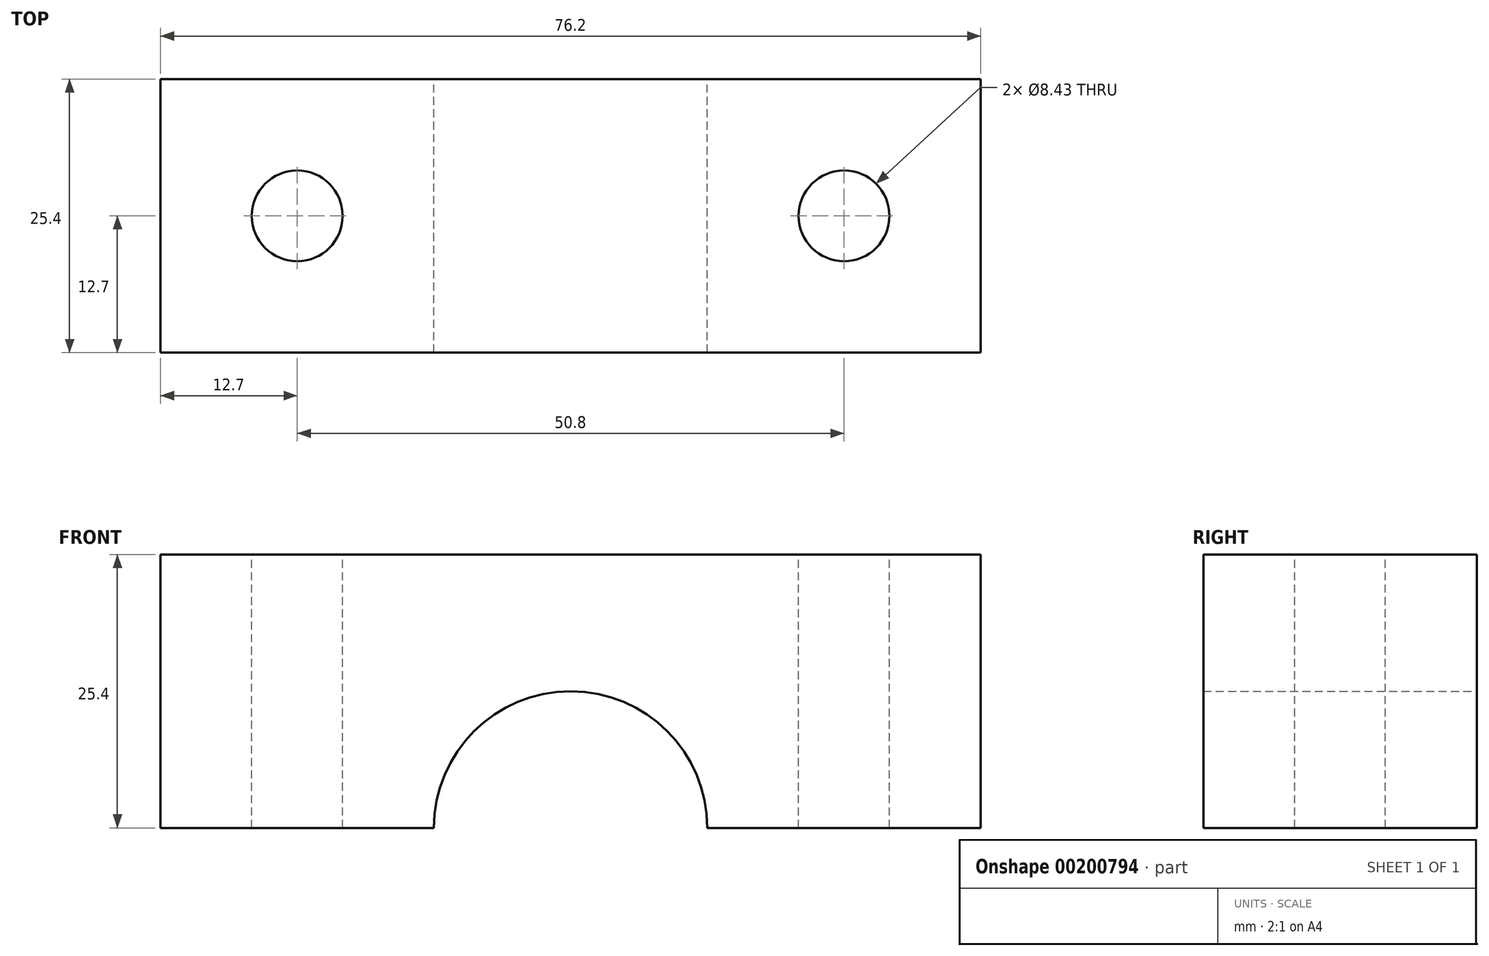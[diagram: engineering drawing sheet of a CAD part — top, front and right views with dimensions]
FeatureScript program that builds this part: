
annotation { "Feature Type Name" : "Feature", "Feature Type Description" : "" }
export const myFeature = defineFeature(function(context is Context, id is Id, definition is map)
    precondition{}
    {
        {
            var Q0;
            Q0=qCreatedBy(makeId("Front.planeOp"),FACE);
            var sketch = newSketch(context, id + "F0", { "sketchPlane" : qUnion([Q0])});
            skLineSegment(sketch, "E0.bottom", {"start": v(0, 0) * mm, "end": v(25.4, 0) * mm});
            skLineSegment(sketch, "E0.top", {"start": v(0, 25.4) * mm, "end": v(76.2, 25.4) * mm});
            skLineSegment(sketch, "E0.left", {"start": v(0, 0) * mm, "end": v(0, 25.4) * mm});
            skLineSegment(sketch, "E0.right", {"start": v(76.2, 0) * mm, "end": v(76.2, 25.4) * mm});
            skArc(sketch, "E1", {"start": v(50.8, 0) * mm, "mid": v(38.1, 12.7) * mm, "end": v(25.4, 0) * mm});
            skLineSegment(sketch, "E2.trimOffspring", {"start": v(50.8, 0) * mm, "end": v(76.2, 0) * mm});
            skSolve(sketch);
        }
        {
            var Q0;
            Q0 = qSketchRegion(id + "F0", true);
            extrude(context, id + "F1", {"entities" : qUnion([Q0]), "depth" : 25.4 * mm});
        }
        {
            var Q0;
            Q0=makeQuery(id+"F1.opExtrude","SWEPT_FACE",FACE,{"disambiguationData":[OSD([sQuery(id+"F0.wireOp",EDGE,"E0.top")])]});
            var sketch = newSketch(context, id + "F2", { "sketchPlane" : qUnion([Q0])});
            skPoint(sketch, "E3", {"position": v(12.7, -12.7) * mm});
            skPoint(sketch, "E4", {"position": v(63.5, -12.7) * mm});
            skSolve(sketch);
        }
        {
            var Q0;
            Q0=sQuery(id+"F2.wireOp",VERTEX,"E3");
            var Q1;
            Q1=sQuery(id+"F2.wireOp",VERTEX,"E4");
            var Q2;
            Q2=makeQuery(id+"F1.opExtrude","SWEPT_BODY",BODY,{"disambiguationData":[OSD([sQuery(id+"F0.wireOp",EDGE,"E0.bottom"),sQuery(id+"F0.wireOp",EDGE,"E0.top"),sQuery(id+"F0.wireOp",EDGE,"E0.left"),sQuery(id+"F0.wireOp",EDGE,"E0.right"),sQuery(id+"F0.wireOp",EDGE,"E1"),sQuery(id+"F0.wireOp",EDGE,"E2.trimOffspring")])]});
            hole(context, id + "F3", {"style" : HoleStyle.SIMPLE, "endStyle" : HoleEndStyle.THROUGH, "standardTappedOrClearance" : lookupTablePath({ "standard" : "ANSI", "fit" : "Normal (ASME)", "size" : "5/16", "type" : "Clearance" }), "standardBlindInLast" : lookupTablePath({ "fit" : "Free", "standard" : "ANSI", "size" : "5/16", "type" : "Clearance" }), "holeDiameter" : 8.43 * mm, "locations" : qUnion([Q0, Q1]), "scope" : qUnion([Q2]), "isTappedThrough" : true});
        }
    });
